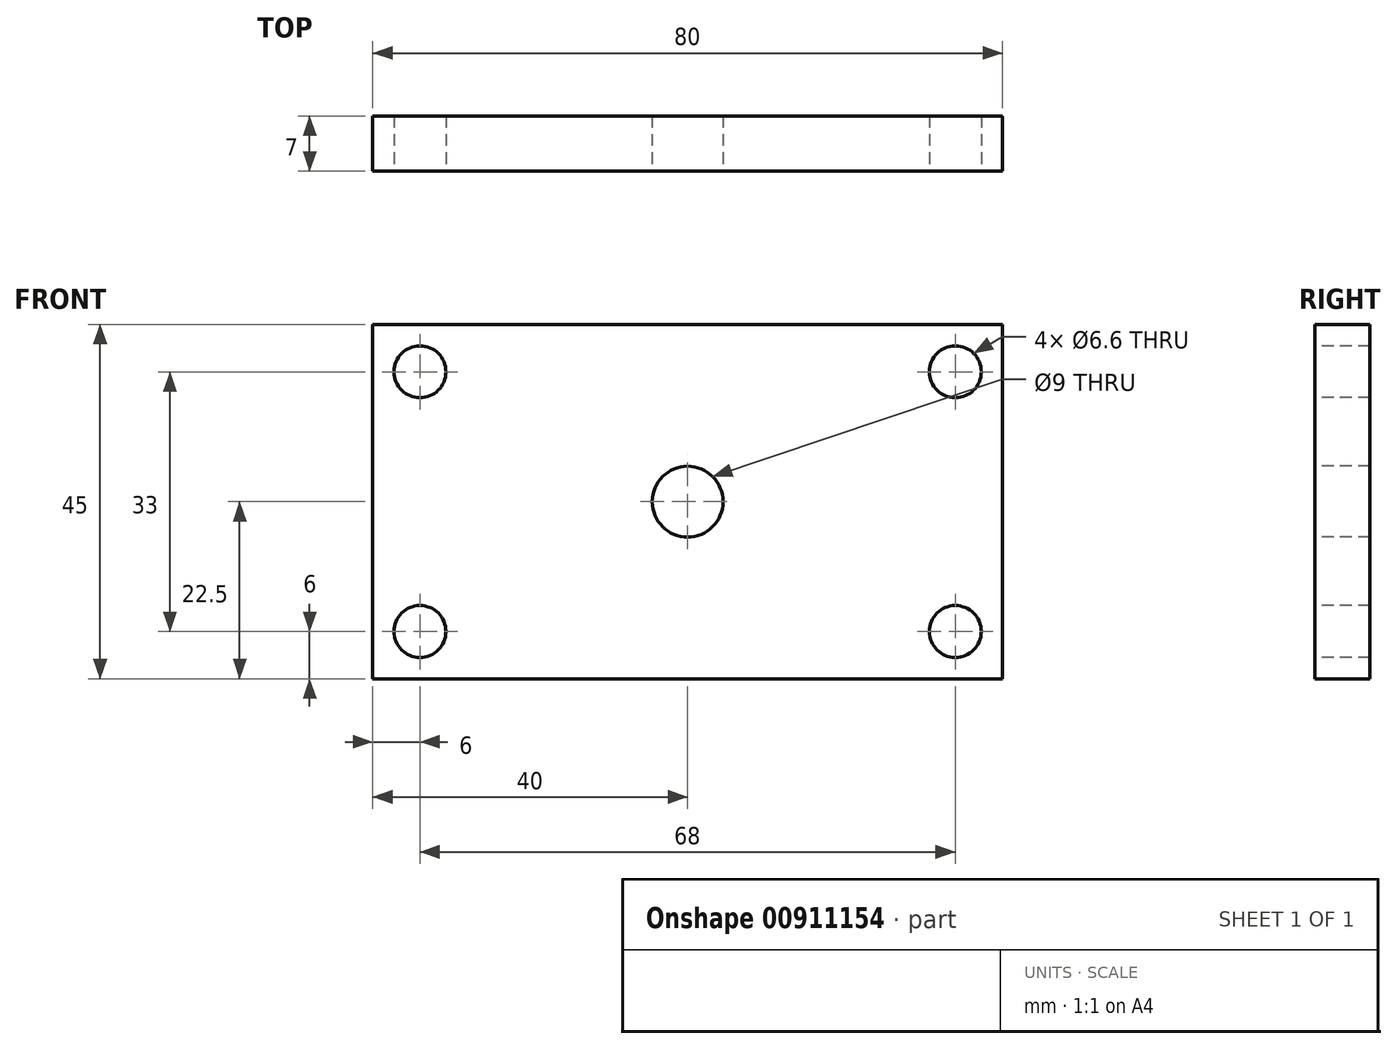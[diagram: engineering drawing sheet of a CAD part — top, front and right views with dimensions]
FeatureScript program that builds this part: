
annotation { "Feature Type Name" : "Feature", "Feature Type Description" : "" }
export const myFeature = defineFeature(function(context is Context, id is Id, definition is map)
    precondition{}
    {
        {
            var Q0;
            Q0=qCreatedBy(makeId("Front.planeOp"),FACE);
            var sketch = newSketch(context, id + "F0", { "sketchPlane" : qUnion([Q0])});
            skLineSegment(sketch, "E0.bottom", {"start": v(-40, 22.5) * mm, "end": v(40, 22.5) * mm});
            skLineSegment(sketch, "E0.left", {"start": v(-40, 22.5) * mm, "end": v(-40, -22.5) * mm});
            skLineSegment(sketch, "E0.right", {"start": v(40, 22.5) * mm, "end": v(40, -22.5) * mm});
            skLineSegment(sketch, "E1", {"start": v(-40, -22.5) * mm, "end": v(40, -22.5) * mm});
            skSolve(sketch);
        }
        {
            var Q0;
            Q0=makeQuery(id+"F0.imprint","IMPRINT",FACE,{"disambiguationData":[TD([[makeQuery(id+"F0.imprint","IMPRINT",EDGE,{"derivedFrom":sQuery(id+"F0.wireOp",EDGE,"E0.bottom")}),-1.0]])]});
            extrude(context, id + "F1", {"entities" : qUnion([Q0]), "depth" : 7 * mm, "offsetDistance" : 25 * mm});
        }
        {
            var Q0;
            Q0=makeQuery(id+"F1.opExtrude","CAP_FACE",FACE,{"disambiguationData":[OSD([sQuery(id+"F0.wireOp",EDGE,"E0.bottom"),sQuery(id+"F0.wireOp",EDGE,"E0.top"),sQuery(id+"F0.wireOp",EDGE,"E0.left"),sQuery(id+"F0.wireOp",EDGE,"E0.right"),sQuery(id+"F0.wireOp",EDGE,"USfBrNj5-NE8k-w3ud-8WRO-zbuGyIkI966C"),sQuery(id+"F0.wireOp",EDGE,"MKWHamnr-gFBu-T2Dl-EdH3-jOcSzT7smLSn"),sQuery(id+"F0.wireOp",EDGE,"d849b05d-fbdd-42a1-bb86-b4805a4f3501.trimOffspring"),sQuery(id+"F0.wireOp",EDGE,"COQGsJRQ-AFBl-ej7y-5W9p-H4CLD0zX3LHm")])],"isStart":false});
            var sketch = newSketch(context, id + "F2", { "sketchPlane" : qUnion([Q0])});
            skCircle(sketch, "E2", {"center": v(34, 16.5) * mm, "radius": 3 * mm});
            skCircle(sketch, "E3.MirrorC", {"center": v(34, -16.5) * mm, "radius": 3 * mm});
            skCircle(sketch, "E4.MirrorC", {"center": v(-34, 16.5) * mm, "radius": 3 * mm});
            skCircle(sketch, "E5.MirrorC", {"center": v(-34, -16.5) * mm, "radius": 3 * mm});
            skSolve(sketch);
        }
        {
            var Q0;
            Q0=sQuery(id+"F2.wireOp",VERTEX,"E4.MirrorC.center");
            var Q1;
            Q1=sQuery(id+"F2.wireOp",VERTEX,"E5.MirrorC.center");
            var Q2;
            Q2=sQuery(id+"F2.wireOp",VERTEX,"E3.MirrorC.center");
            var Q3;
            Q3=sQuery(id+"F2.wireOp",VERTEX,"E2.center");
            var Q4;
            Q4=makeQuery(id+"F1.opExtrude","SWEPT_BODY",BODY,{"disambiguationData":[OSD([sQuery(id+"F0.wireOp",EDGE,"E0.bottom"),sQuery(id+"F0.wireOp",EDGE,"E0.top"),sQuery(id+"F0.wireOp",EDGE,"E0.left"),sQuery(id+"F0.wireOp",EDGE,"E0.right"),sQuery(id+"F0.wireOp",EDGE,"USfBrNj5-NE8k-w3ud-8WRO-zbuGyIkI966C"),sQuery(id+"F0.wireOp",EDGE,"MKWHamnr-gFBu-T2Dl-EdH3-jOcSzT7smLSn"),sQuery(id+"F0.wireOp",EDGE,"d849b05d-fbdd-42a1-bb86-b4805a4f3501.trimOffspring"),sQuery(id+"F0.wireOp",EDGE,"COQGsJRQ-AFBl-ej7y-5W9p-H4CLD0zX3LHm")])]});
            hole(context, id + "F3", {"style" : HoleStyle.SIMPLE, "endStyle" : HoleEndStyle.THROUGH, "standardTappedOrClearance" : lookupTablePath({ "fit" : "Normal", "standard" : "ISO", "size" : "M6", "type" : "Clearance" }), "standardBlindInLast" : lookupTablePath({ "fit" : "Normal", "standard" : "ISO", "size" : "M6", "type" : "Clearance" }), "holeDiameter" : 6.6 * mm, "majorDiameter" : 5 * mm, "isTappedThrough" : true, "tappedDepth" : 12 * mm, "tapClearance" : 3, "locations" : qUnion([Q0, Q1, Q2, Q3]), "scope" : qUnion([Q4])});
        }
        {
            var Q0;
            Q0=makeQuery(id+"F1.opExtrude","CAP_FACE",FACE,{"disambiguationData":[OSD([sQuery(id+"F0.wireOp",EDGE,"E0.bottom"),sQuery(id+"F0.wireOp",EDGE,"E0.left"),sQuery(id+"F0.wireOp",EDGE,"E0.right"),sQuery(id+"F0.wireOp",EDGE,"E1")])],"isStart":false});
            var sketch = newSketch(context, id + "F4", { "sketchPlane" : qUnion([Q0])});
            skCircle(sketch, "E6", {"center": v(0, 0) * mm, "radius": 4.5 * mm});
            skSolve(sketch);
        }
        {
            var Q0;
            Q0=sQuery(id+"F4.wireOp",VERTEX,"E6.center");
            var Q1;
            Q1=makeQuery(id+"F1.opExtrude","SWEPT_BODY",BODY,{"disambiguationData":[OSD([sQuery(id+"F0.wireOp",EDGE,"E0.bottom"),sQuery(id+"F0.wireOp",EDGE,"E0.left"),sQuery(id+"F0.wireOp",EDGE,"E0.right"),sQuery(id+"F0.wireOp",EDGE,"E1")])]});
            hole(context, id + "F5", {"style" : HoleStyle.SIMPLE, "endStyle" : HoleEndStyle.THROUGH, "standardTappedOrClearance" : lookupTablePath({ "fit" : "Normal", "standard" : "ISO", "size" : "M8", "type" : "Clearance" }), "standardBlindInLast" : lookupTablePath({ "fit" : "Normal", "standard" : "ISO", "size" : "M8", "type" : "Clearance" }), "holeDiameter" : 9 * mm, "majorDiameter" : 5 * mm, "isTappedThrough" : true, "tappedDepth" : 12 * mm, "tapClearance" : 3, "locations" : qUnion([Q0]), "scope" : qUnion([Q1])});
        }
    });
